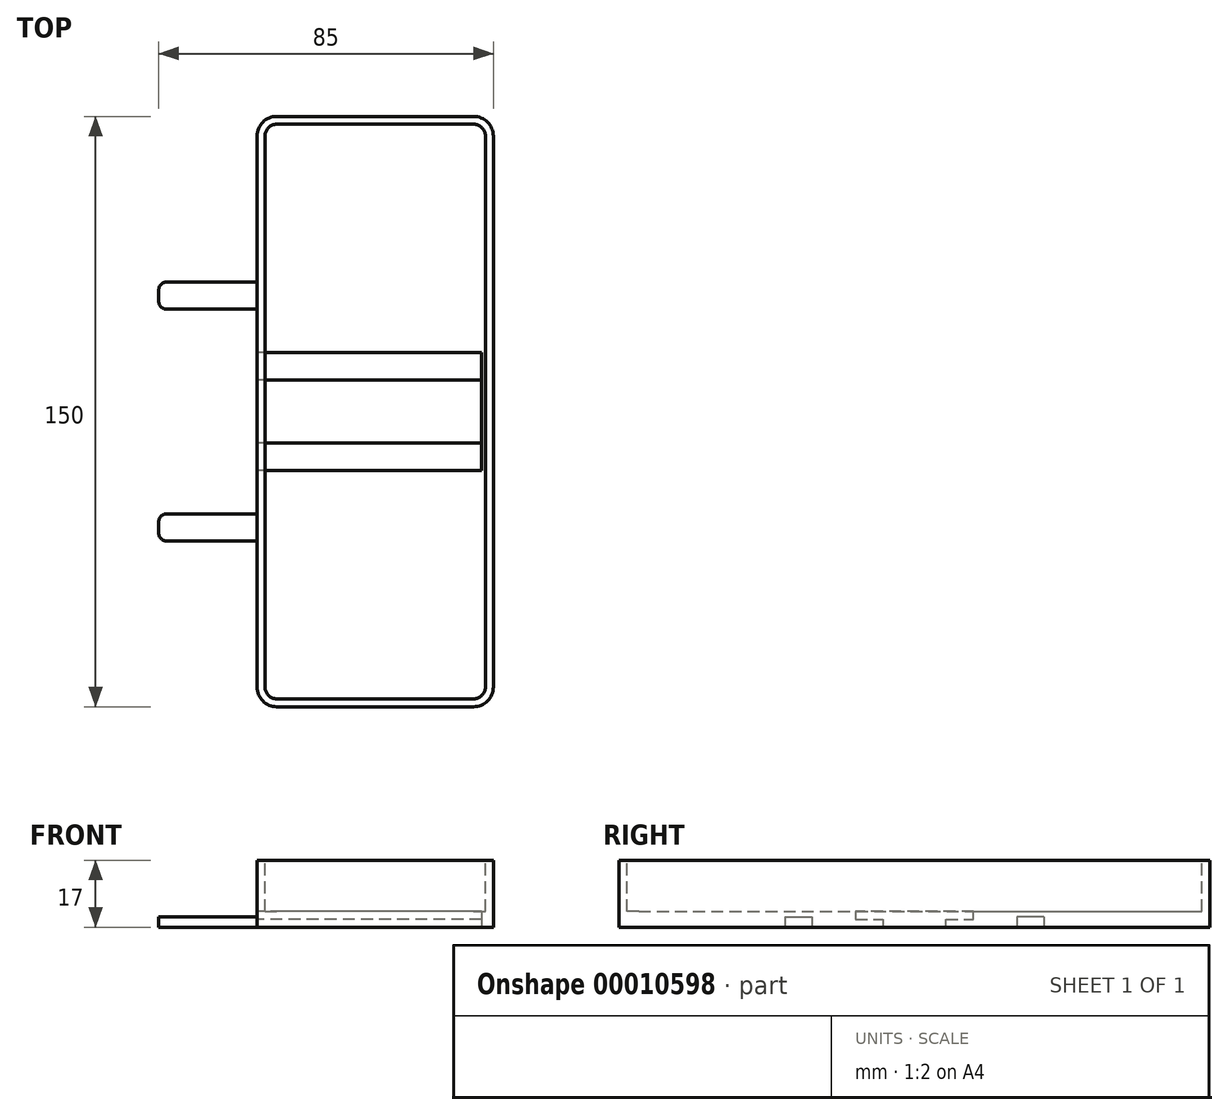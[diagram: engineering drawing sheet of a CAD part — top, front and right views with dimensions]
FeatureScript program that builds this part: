
annotation { "Feature Type Name" : "Feature", "Feature Type Description" : "" }
export const myFeature = defineFeature(function(context is Context, id is Id, definition is map)
    precondition{}
    {
        {
            var Q0;
            Q0=qCreatedBy(makeId("Front.planeOp"),FACE);
            var sketch = newSketch(context, id + "F0", { "sketchPlane" : qUnion([Q0])});
            skLineSegment(sketch, "E0.bottom", {"start": v(0, 0) * mm, "end": v(-60, 0) * mm});
            skLineSegment(sketch, "E0.top", {"start": v(0, 17) * mm, "end": v(-60, 17) * mm});
            skLineSegment(sketch, "E0.left", {"start": v(0, 0) * mm, "end": v(0, 17) * mm});
            skLineSegment(sketch, "E0.right", {"start": v(-60, 0) * mm, "end": v(-60, 17) * mm});
            skSolve(sketch);
        }
        {
            var Q0;
            Q0=makeQuery(id+"F0.imprint","IMPRINT",FACE,{"disambiguationData":[TD([[makeQuery(id+"F0.imprint","IMPRINT",EDGE,{"derivedFrom":sQuery(id+"F0.wireOp",EDGE,"E0.bottom")}),-1.0]])]});
            extrude(context, id + "F1", {"entities" : qUnion([Q0]), "depth" : 150 * mm});
        }
        {
            var Q0;
            Q0=makeQuery(id+"F1.opExtrude","SWEPT_FACE",FACE,{"disambiguationData":[OSD([sQuery(id+"F0.wireOp",EDGE,"E0.top")])]});
            shell(context, id + "F2", {"entities" : qUnion([Q0]), "thickness" : 4 * mm});
        }
        {
            var Q0;
            Q0=makeQuery(id+"F1.opExtrude","SWEPT_FACE",FACE,{"disambiguationData":[OSD([sQuery(id+"F0.wireOp",EDGE,"E0.right")])]});
            var sketch = newSketch(context, id + "F3", { "sketchPlane" : qUnion([Q0])});
            skLineSegment(sketch, "E1.bottom", {"start": v(42.1, 2.6) * mm, "end": v(49, 2.6) * mm});
            skLineSegment(sketch, "E1.top", {"start": v(42.1, 0) * mm, "end": v(49, 0) * mm});
            skLineSegment(sketch, "E1.left", {"start": v(42.1, 2.6) * mm, "end": v(42.1, 0) * mm});
            skLineSegment(sketch, "E1.right", {"start": v(49, 2.6) * mm, "end": v(49, 0) * mm});
            skLineSegment(sketch, "E2", {"start": v(75, 17) * mm, "end": v(75, -3.76) * mm, "construction": true});
            skLineSegment(sketch, "E3.0.MirrorCS", {"start": v(107.9, 2.6) * mm, "end": v(107.9, 0) * mm});
            skLineSegment(sketch, "E4.0.MirrorCS", {"start": v(107.9, 2.6) * mm, "end": v(101, 2.6) * mm});
            skLineSegment(sketch, "E5.0.MirrorCS", {"start": v(107.9, 0) * mm, "end": v(101, 0) * mm});
            skLineSegment(sketch, "E6.0.MirrorCS", {"start": v(101, 2.6) * mm, "end": v(101, 0) * mm});
            skLineSegment(sketch, "E7", {"start": v(67, 0) * mm, "end": v(67, 2) * mm});
            skLineSegment(sketch, "E8", {"start": v(67, 2) * mm, "end": v(60, 2) * mm});
            skLineSegment(sketch, "E9", {"start": v(60, 2) * mm, "end": v(60, 4) * mm});
            skLineSegment(sketch, "E10", {"start": v(90, 4) * mm, "end": v(90, 2) * mm});
            skLineSegment(sketch, "E11", {"start": v(90, 2) * mm, "end": v(83, 2) * mm});
            skLineSegment(sketch, "E12", {"start": v(83, 2) * mm, "end": v(83, 0) * mm});
            skLineSegment(sketch, "E13", {"start": v(83, 0) * mm, "end": v(67, 0) * mm});
            skLineSegment(sketch, "E14", {"start": v(60, 4) * mm, "end": v(90, 4) * mm});
            skSolve(sketch);
        }
        {
            var Q0;
            Q0=makeQuery(id+"F1.opExtrude","CAP_EDGE",EDGE,{"disambiguationData":[OSD([sQuery(id+"F0.wireOp",EDGE,"E0.right")])],"isStart":true});
            var Q1;
            Q1=makeQuery(id+"F1.opExtrude","CAP_EDGE",EDGE,{"disambiguationData":[OSD([sQuery(id+"F0.wireOp",EDGE,"E0.right")])],"isStart":false});
            var Q2;
            Q2=makeQuery(id+"F1.opExtrude","CAP_EDGE",EDGE,{"disambiguationData":[OSD([sQuery(id+"F0.wireOp",EDGE,"E0.left")])],"isStart":false});
            var Q3;
            Q3=makeQuery(id+"F1.opExtrude","CAP_EDGE",EDGE,{"disambiguationData":[OSD([sQuery(id+"F0.wireOp",EDGE,"E0.left")])],"isStart":true});
            var Q4;
            {var subQ0=sQuery(id+"F0.wireOp",EDGE,"E0.right");Q4=makeQuery(id+"F2.opShell","OFFSET_EDGE",EDGE,{"disambiguationData":[OSD([subQ0]),TDD([makeQuery(id+"F1.opExtrude","CAP_EDGE",EDGE,{"disambiguationData":[OSD([subQ0])],"isStart":false})])]});}
            var Q5;
            {var subQ0=sQuery(id+"F0.wireOp",EDGE,"E0.left");Q5=makeQuery(id+"F2.opShell","OFFSET_EDGE",EDGE,{"disambiguationData":[OSD([subQ0]),TDD([makeQuery(id+"F1.opExtrude","CAP_EDGE",EDGE,{"disambiguationData":[OSD([subQ0])],"isStart":false})])]});}
            var Q6;
            {var subQ0=sQuery(id+"F0.wireOp",EDGE,"E0.right");Q6=makeQuery(id+"F2.opShell","OFFSET_EDGE",EDGE,{"disambiguationData":[OSD([subQ0]),TDD([makeQuery(id+"F1.opExtrude","CAP_EDGE",EDGE,{"disambiguationData":[OSD([subQ0])],"isStart":true})])]});}
            var Q7;
            {var subQ0=sQuery(id+"F0.wireOp",EDGE,"E0.left");Q7=makeQuery(id+"F2.opShell","OFFSET_EDGE",EDGE,{"disambiguationData":[OSD([subQ0]),TDD([makeQuery(id+"F1.opExtrude","CAP_EDGE",EDGE,{"disambiguationData":[OSD([subQ0])],"isStart":true})])]});}
            fillet(context, id + "F4", {"entities" : qUnion([Q0, Q1, Q2, Q3, Q4, Q5, Q6, Q7]), "radius" : 5 * mm, "tangentPropagation" : true, "allowEdgeOverflow" : false});
        }
        {
            var Q0;
            Q0=makeQuery(id+"F3.imprint","IMPRINT",FACE,{"disambiguationData":[TD([[makeQuery(id+"F3.imprint","IMPRINT",EDGE,{"derivedFrom":sQuery(id+"F3.wireOp",EDGE,"E1.bottom")}),-1.0]])]});
            var Q1;
            Q1=makeQuery(id+"F3.imprint","IMPRINT",FACE,{"disambiguationData":[TD([[makeQuery(id+"F3.imprint","IMPRINT",EDGE,{"derivedFrom":sQuery(id+"F3.wireOp",EDGE,"E3.0.MirrorCS")}),-1.0]])]});
            extrude(context, id + "F5", {"entities" : qUnion([Q0, Q1]), "operationType" : NewBodyOperationType.ADD, "depth" : 25 * mm});
        }
        {
            var Q0;
            Q0=makeQuery(id+"F5.opExtrude","CAP_EDGE",EDGE,{"disambiguationData":[OSD([sQuery(id+"F3.wireOp",EDGE,"E1.left")])],"isStart":false});
            var Q1;
            Q1=makeQuery(id+"F5.opExtrude","CAP_EDGE",EDGE,{"disambiguationData":[OSD([sQuery(id+"F3.wireOp",EDGE,"E1.right")])],"isStart":false});
            var Q2;
            Q2=makeQuery(id+"F5.opExtrude","CAP_EDGE",EDGE,{"disambiguationData":[OSD([sQuery(id+"F3.wireOp",EDGE,"E6.0.MirrorCS")])],"isStart":false});
            var Q3;
            Q3=makeQuery(id+"F5.opExtrude","CAP_EDGE",EDGE,{"disambiguationData":[OSD([sQuery(id+"F3.wireOp",EDGE,"E3.0.MirrorCS")])],"isStart":false});
            fillet(context, id + "F6", {"entities" : qUnion([Q0, Q1, Q2, Q3]), "radius" : 2 * mm, "tangentPropagation" : true, "allowEdgeOverflow" : false});
        }
        {
            var Q0;
            Q0=makeQuery(id+"F3.imprint","IMPRINT",FACE,{"disambiguationData":[TD([[makeQuery(id+"F3.imprint","IMPRINT",EDGE,{"derivedFrom":sQuery(id+"F3.wireOp",EDGE,"E7")}),-1.0]])]});
            extrude(context, id + "F7", {"entities" : qUnion([Q0]), "operationType" : NewBodyOperationType.REMOVE, "oppositeDirection" : true, "depth" : 57 * mm});
        }
        {
            var Q0;
            Q0=makeQuery(id+"F1.opExtrude","SWEPT_FACE",FACE,{"disambiguationData":[OSD([sQuery(id+"F0.wireOp",EDGE,"E0.top")])]});
            var sketch = newSketch(context, id + "F8", { "sketchPlane" : qUnion([Q0])});
            skLineSegment(sketch, "E15.0", {"start": v(-2, -145) * mm, "end": v(-2, -5) * mm});
            skLineSegment(sketch, "E15.1", {"start": v(-5, -148) * mm, "end": v(-55, -148) * mm});
            skLineSegment(sketch, "E15.2", {"start": v(-58, -145) * mm, "end": v(-58, -5) * mm});
            skLineSegment(sketch, "E15.3", {"start": v(-5, -2) * mm, "end": v(-55, -2) * mm});
            skPoint(sketch, "E16.visualSharp", {"position": v(-2, -2) * mm});
            skArc(sketch, "E16.filletArc", {"start": v(-2, -5) * mm, "mid": v(-2.88, -2.88) * mm, "end": v(-5, -2) * mm});
            skPoint(sketch, "E17.visualSharp", {"position": v(-58, -2) * mm});
            skArc(sketch, "E17.filletArc", {"start": v(-55, -2) * mm, "mid": v(-57.12, -2.88) * mm, "end": v(-58, -5) * mm});
            skPoint(sketch, "E18.visualSharp", {"position": v(-58, -148) * mm});
            skArc(sketch, "E18.filletArc", {"start": v(-58, -145) * mm, "mid": v(-57.12, -147.12) * mm, "end": v(-55, -148) * mm});
            skPoint(sketch, "E19.visualSharp", {"position": v(-2, -148) * mm});
            skArc(sketch, "E19.filletArc", {"start": v(-5, -148) * mm, "mid": v(-2.88, -147.12) * mm, "end": v(-2, -145) * mm});
            skSolve(sketch);
        }
        {
            var Q0;
            Q0=makeQuery(id+"F8.imprint","IMPRINT",FACE,{"disambiguationData":[TD([[makeQuery(id+"F8.imprint","IMPRINT",EDGE,{"derivedFrom":sQuery(id+"F8.wireOp",EDGE,"E15.0")}),1.0]])]});
            extrude(context, id + "F9", {"entities" : qUnion([Q0]), "operationType" : NewBodyOperationType.REMOVE, "oppositeDirection" : true, "depth" : 13 * mm});
        }
    });
